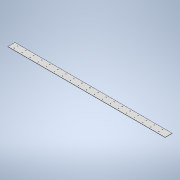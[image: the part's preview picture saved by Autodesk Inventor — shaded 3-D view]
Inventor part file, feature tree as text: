
AUTODESK INVENTOR PART (.ipt)
format: ipt  version: 2022 (Build 260153000, 153)  size: 164,352 bytes
history: native  units: mm
features: sheet_metal_op x1, sketch x1, other x1
ambient origin geometry x8: Origin, YZ Plane, XZ Plane, XY Plane, X Axis, Y Axis, Z Axis, Center Point
bodies: Body1 (feature_tree)
feature tree (3):
  sheet_metal_op  "Face3"
  sketch  "Sketch1"  dims[d0=44.0mm d1=978.0mm d2=11.0mm d3=28.0mm d4=3.35mm d5=190.0mm d7=50.0mm d8=20.0mm d10=22.0mm d15=1.5mm]
  other  "Plate3"
